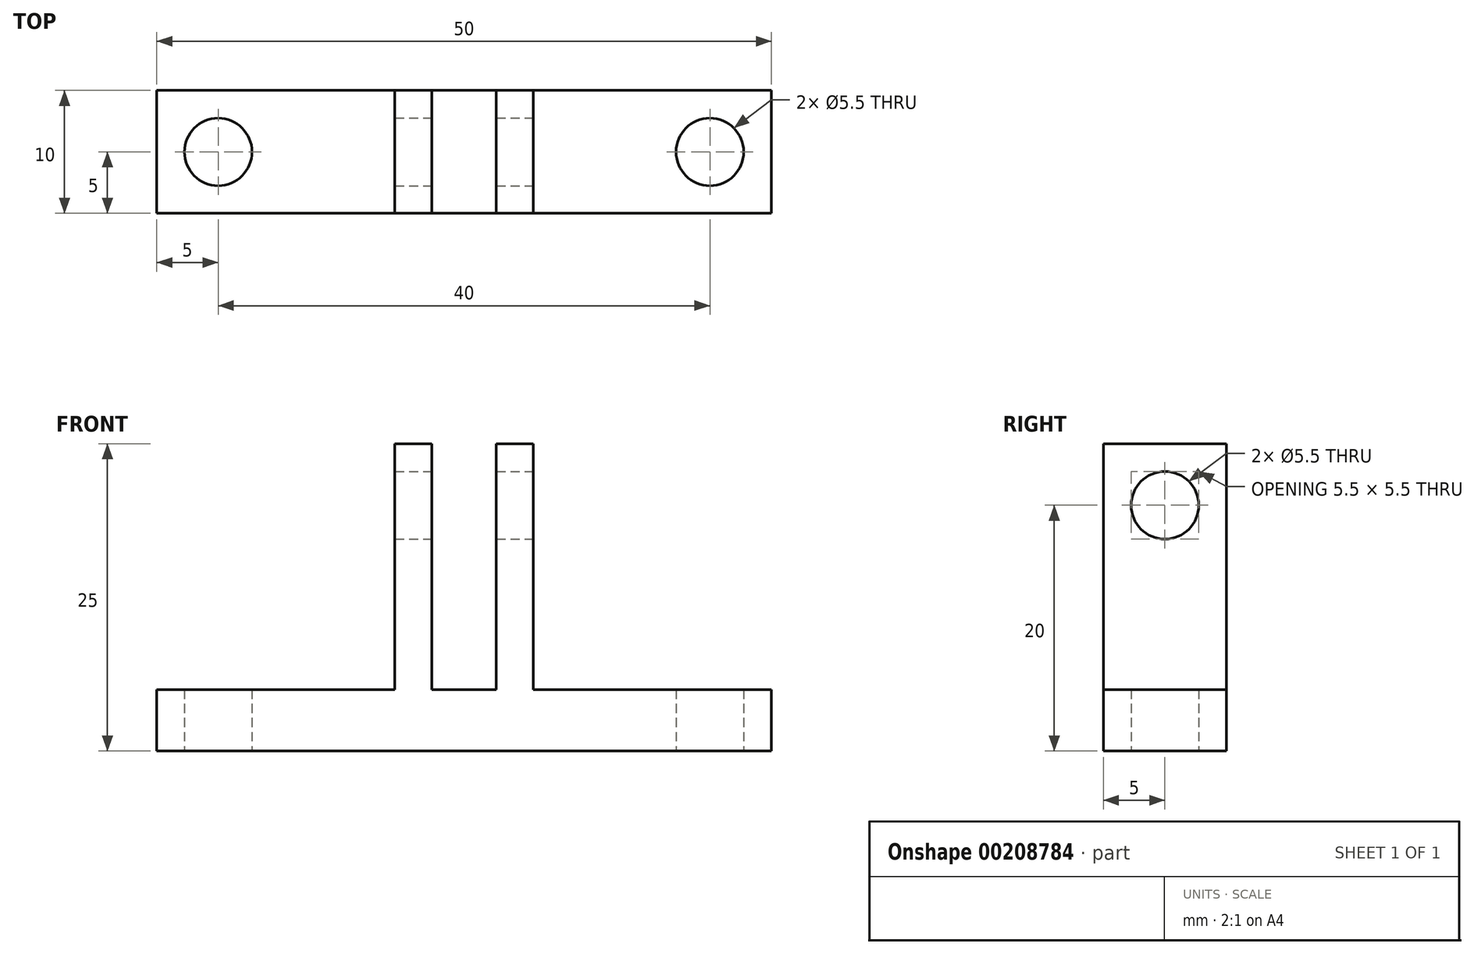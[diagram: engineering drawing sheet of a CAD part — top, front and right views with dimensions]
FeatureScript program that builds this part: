
annotation { "Feature Type Name" : "Feature", "Feature Type Description" : "" }
export const myFeature = defineFeature(function(context is Context, id is Id, definition is map)
    precondition{}
    {
        {
            var Q0;
            Q0=qCreatedBy(makeId("Top.planeOp"),FACE);
            var sketch = newSketch(context, id + "F0", { "sketchPlane" : qUnion([Q0])});
            skLineSegment(sketch, "E0.bottom", {"start": v(25, -5) * mm, "end": v(-25, -5) * mm});
            skLineSegment(sketch, "E0.top", {"start": v(25, 5) * mm, "end": v(-25, 5) * mm});
            skLineSegment(sketch, "E0.left", {"start": v(25, -5) * mm, "end": v(25, 5) * mm});
            skLineSegment(sketch, "E0.right", {"start": v(-25, -5) * mm, "end": v(-25, 5) * mm});
            skPoint(sketch, "E0.middle", {"position": v(0, 0) * mm});
            skSolve(sketch);
        }
        {
            var Q0;
            Q0=makeQuery(id+"F0.imprint","IMPRINT",FACE,{"disambiguationData":[TD([[makeQuery(id+"F0.imprint","IMPRINT",EDGE,{"derivedFrom":sQuery(id+"F0.wireOp",EDGE,"E0.bottom")}),-1.0]])]});
            extrude(context, id + "F1", {"entities" : qUnion([Q0]), "depth" : 5 * mm});
        }
        {
            var Q0;
            Q0=makeQuery(id+"F1.opExtrude","CAP_FACE",FACE,{"disambiguationData":[OSD([sQuery(id+"F0.wireOp",EDGE,"E0.bottom"),sQuery(id+"F0.wireOp",EDGE,"E0.top"),sQuery(id+"F0.wireOp",EDGE,"E0.left"),sQuery(id+"F0.wireOp",EDGE,"E0.right")])],"isStart":false});
            var sketch = newSketch(context, id + "F2", { "sketchPlane" : qUnion([Q0])});
            skPoint(sketch, "E1", {"position": v(-20, 0) * mm});
            skPoint(sketch, "E2", {"position": v(20, 0) * mm});
            skSolve(sketch);
        }
        {
            var Q0;
            Q0=sQuery(id+"F2.wireOp",VERTEX,"E1");
            var Q1;
            Q1=sQuery(id+"F2.wireOp",VERTEX,"E2");
            var Q2;
            Q2=makeQuery(id+"F1.opExtrude","SWEPT_BODY",BODY,{"disambiguationData":[OSD([sQuery(id+"F0.wireOp",EDGE,"E0.bottom"),sQuery(id+"F0.wireOp",EDGE,"E0.top"),sQuery(id+"F0.wireOp",EDGE,"E0.left"),sQuery(id+"F0.wireOp",EDGE,"E0.right")])]});
            hole(context, id + "F3", {"style" : HoleStyle.SIMPLE, "endStyle" : HoleEndStyle.THROUGH, "standardTappedOrClearance" : lookupTablePath({ "standard" : "ISO", "fit" : "Normal", "size" : "M5", "type" : "Clearance" }), "standardBlindInLast" : lookupTablePath({ "fit" : "Standard", "standard" : "ISO", "size" : "M5", "type" : "Clearance" }), "holeDiameter" : 5.5 * mm, "locations" : qUnion([Q0, Q1]), "scope" : qUnion([Q2]), "isTappedThrough" : true});
        }
        {
            var Q0;
            Q0=makeQuery(id+"F1.opExtrude","CAP_FACE",FACE,{"disambiguationData":[OSD([sQuery(id+"F0.wireOp",EDGE,"E0.bottom"),sQuery(id+"F0.wireOp",EDGE,"E0.top"),sQuery(id+"F0.wireOp",EDGE,"E0.left"),sQuery(id+"F0.wireOp",EDGE,"E0.right")])],"isStart":false});
            var sketch = newSketch(context, id + "F4", { "sketchPlane" : qUnion([Q0])});
            skLineSegment(sketch, "E3.bottom", {"start": v(2.63, -5) * mm, "end": v(-2.62, -5) * mm, "construction": true});
            skLineSegment(sketch, "E3.top", {"start": v(2.62, 5) * mm, "end": v(-2.63, 5) * mm, "construction": true});
            skLineSegment(sketch, "E3.left", {"start": v(2.63, -5) * mm, "end": v(2.62, 5) * mm});
            skLineSegment(sketch, "E3.right", {"start": v(-2.62, -5) * mm, "end": v(-2.62, 5) * mm});
            skPoint(sketch, "E3.middle", {"position": v(0, 0) * mm});
            skLineSegment(sketch, "E4.bottom", {"start": v(-2.63, 5) * mm, "end": v(-5.63, 5) * mm});
            skLineSegment(sketch, "E4.top", {"start": v(-2.62, -5) * mm, "end": v(-5.62, -5) * mm});
            skLineSegment(sketch, "E4.left", {"start": v(-2.63, 5) * mm, "end": v(-2.62, -5) * mm});
            skLineSegment(sketch, "E4.right", {"start": v(-5.63, 5) * mm, "end": v(-5.62, -5) * mm});
            skLineSegment(sketch, "E5.bottom", {"start": v(2.62, 5) * mm, "end": v(5.62, 5) * mm});
            skLineSegment(sketch, "E5.top", {"start": v(2.63, -5) * mm, "end": v(5.63, -5) * mm});
            skLineSegment(sketch, "E5.left", {"start": v(2.62, 5) * mm, "end": v(2.63, -5) * mm});
            skLineSegment(sketch, "E5.right", {"start": v(5.62, 5) * mm, "end": v(5.63, -5) * mm});
            skSolve(sketch);
        }
        {
            var Q0;
            Q0=makeQuery(id+"F4.imprint","IMPRINT",FACE,{"disambiguationData":[TD([[makeQuery(id+"F4.imprint","IMPRINT",EDGE,{"derivedFrom":sQuery(id+"F4.wireOp",EDGE,"E4.bottom")}),1.0]])]});
            var Q1;
            Q1=makeQuery(id+"F4.imprint","IMPRINT",FACE,{"disambiguationData":[TD([[makeQuery(id+"F4.imprint","IMPRINT",EDGE,{"derivedFrom":sQuery(id+"F4.wireOp",EDGE,"E5.bottom")}),1.0]])]});
            var Q2;
            Q2=sQuery(id+"F4.wireOp",EDGE,"E3.top");
            var Q3;
            Q3=sQuery(id+"F4.wireOp",EDGE,"E3.bottom");
            extrude(context, id + "F5", {"entities" : qUnion([Q0, Q1]), "operationType" : NewBodyOperationType.ADD, "surfaceEntities" : qUnion([Q2, Q3]), "depth" : 20 * mm});
        }
        {
            var Q0;
            Q0=makeQuery(id+"F5.opExtrude","SWEPT_FACE",FACE,{"disambiguationData":[OSD([sQuery(id+"F4.wireOp",EDGE,"E4.right")])]});
            var sketch = newSketch(context, id + "F6", { "sketchPlane" : qUnion([Q0])});
            skPoint(sketch, "E6", {"position": v(0, 20) * mm});
            skSolve(sketch);
        }
        {
            var Q0;
            Q0=sQuery(id+"F6.wireOp",VERTEX,"E6");
            var Q1;
            Q1=makeQuery(id+"F1.opExtrude","SWEPT_BODY",BODY,{"disambiguationData":[OSD([sQuery(id+"F0.wireOp",EDGE,"E0.bottom"),sQuery(id+"F0.wireOp",EDGE,"E0.top"),sQuery(id+"F0.wireOp",EDGE,"E0.left"),sQuery(id+"F0.wireOp",EDGE,"E0.right")])]});
            hole(context, id + "F7", {"style" : HoleStyle.SIMPLE, "endStyle" : HoleEndStyle.THROUGH, "standardTappedOrClearance" : lookupTablePath({ "standard" : "ISO", "fit" : "Normal", "size" : "M5", "type" : "Clearance" }), "standardBlindInLast" : lookupTablePath({ "fit" : "Standard", "standard" : "ISO", "size" : "M5", "type" : "Clearance" }), "holeDiameter" : 5.5 * mm, "locations" : qUnion([Q0]), "scope" : qUnion([Q1]), "isTappedThrough" : true});
        }
    });
